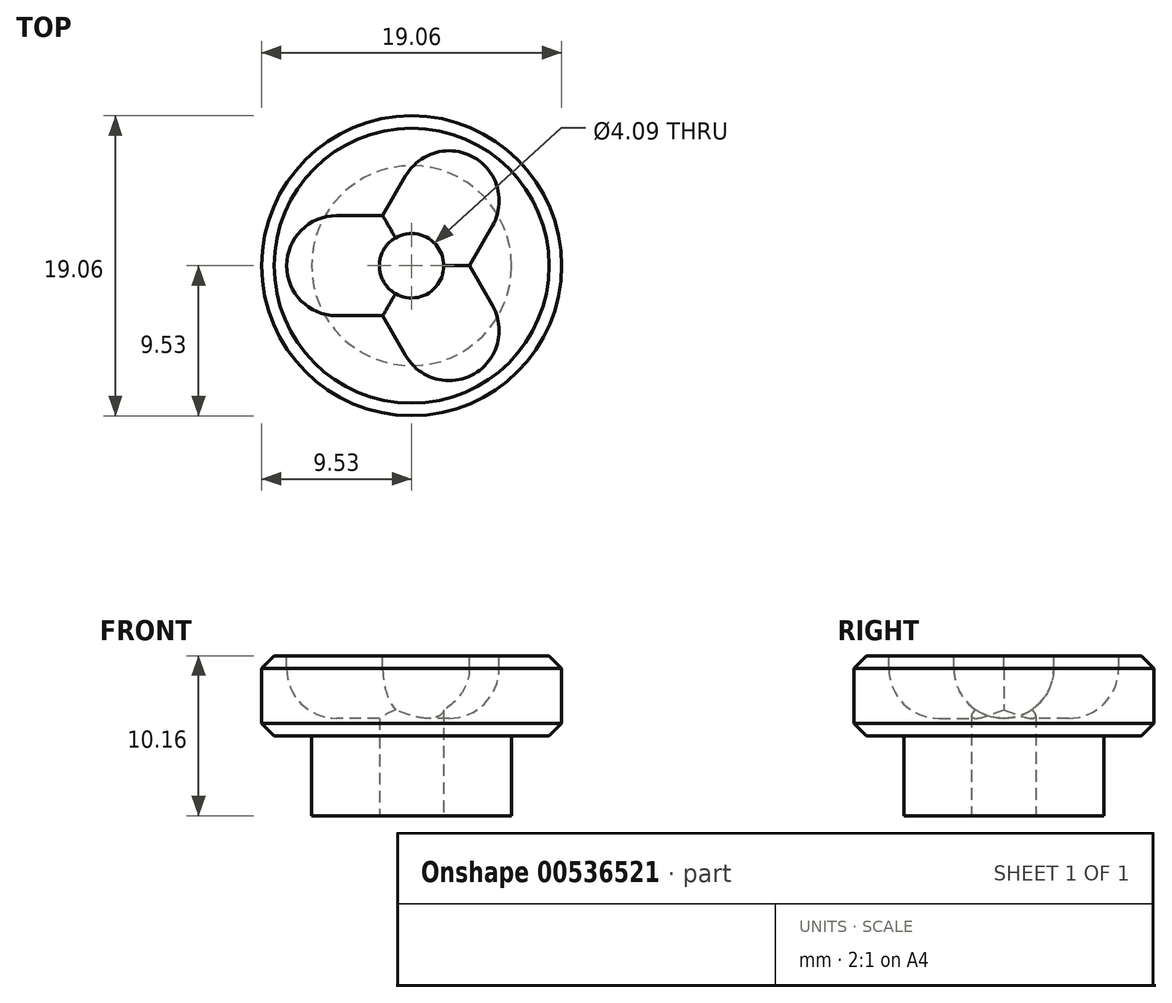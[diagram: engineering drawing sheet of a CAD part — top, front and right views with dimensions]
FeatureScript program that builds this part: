
annotation { "Feature Type Name" : "Feature", "Feature Type Description" : "" }
export const myFeature = defineFeature(function(context is Context, id is Id, definition is map)
    precondition{}
    {
        {
            var Q0;
            Q0=qCreatedBy(makeId("Front.planeOp"),FACE);
            var sketch = newSketch(context, id + "F0", { "sketchPlane" : qUnion([Q0])});
            skLineSegment(sketch, "E0", {"start": v(0, 14.96) * mm, "end": v(0, -17.01) * mm, "construction": true});
            skLineSegment(sketch, "E1", {"start": v(0, -10.16) * mm, "end": v(-6.35, -10.16) * mm});
            skLineSegment(sketch, "E2", {"start": v(-6.35, -10.16) * mm, "end": v(-6.35, -5.08) * mm});
            skLineSegment(sketch, "E3", {"start": v(-6.35, -5.08) * mm, "end": v(-9.52, -5.08) * mm});
            skLineSegment(sketch, "E4", {"start": v(-9.52, -5.08) * mm, "end": v(-9.52, 0) * mm});
            skLineSegment(sketch, "E5", {"start": v(-9.52, 0) * mm, "end": v(0, 0) * mm});
            skLineSegment(sketch, "E6", {"start": v(0, 0) * mm, "end": v(0, -10.16) * mm});
            skCircle(sketch, "E7", {"center": v(0, 4.53) * mm, "radius": 3.97 * mm, "construction": true});
            skCircle(sketch, "E8", {"center": v(-4.76, -0.8) * mm, "radius": 3.18 * mm, "construction": true});
            skLineSegment(sketch, "E9", {"start": v(-7.94, 0) * mm, "end": v(-7.94, -3.97) * mm, "construction": true});
            skLineSegment(sketch, "E10", {"start": v(-7.94, -3.97) * mm, "end": v(0, -3.97) * mm, "construction": true});
            skSolve(sketch);
        }
        {
            var Q0;
            Q0=makeQuery(id+"F0.imprint","IMPRINT",FACE,{"disambiguationData":[TD([[makeQuery(id+"F0.imprint","IMPRINT",EDGE,{"derivedFrom":sQuery(id+"F0.wireOp",EDGE,"E1")}),-1.0]])]});
            var Q1;
            Q1=sQuery(id+"F0.wireOp",EDGE,"E0");
            revolve(context, id + "F1", {"entities" : qUnion([Q0]), "axis" : qUnion([Q1]), "revolveType" : RevolveType.FULL});
        }
        {
            var Q0;
            Q0=makeQuery(id+"F1.opRevolve","SWEPT_EDGE",EDGE,{"disambiguationData":[OSD([sQuery(id+"F0.wireOp",EDGE,"E4"),sQuery(id+"F0.wireOp",EDGE,"E5")])]});
            var Q1;
            Q1=makeQuery(id+"F1.opRevolve","SWEPT_EDGE",EDGE,{"disambiguationData":[OSD([sQuery(id+"F0.wireOp",EDGE,"E3"),sQuery(id+"F0.wireOp",EDGE,"E4")])]});
            chamfer(context, id + "F2", {"entities" : qUnion([Q0, Q1]), "width" : 0.8 * mm, "tangentPropagation" : true});
        }
        {
            var Q0;
            Q0=makeQuery(id+"F1.opRevolve","SWEPT_FACE",FACE,{"disambiguationData":[OSD([sQuery(id+"F0.wireOp",EDGE,"E5")])]});
            var sketch = newSketch(context, id + "F3", { "sketchPlane" : qUnion([Q0])});
            skLineSegment(sketch, "E11", {"start": v(-1.83, -3.18) * mm, "end": v(-4.76, -3.18) * mm});
            skArc(sketch, "E12", {"start": v(-4.76, -3.18) * mm, "mid": v(-7.94, 0) * mm, "end": v(-4.76, 3.17) * mm});
            skLineSegment(sketch, "E13", {"start": v(-4.76, 3.18) * mm, "end": v(-1.83, 3.18) * mm});
            skLineSegment(sketch, "E14", {"start": v(-1.83, 3.18) * mm, "end": v(-0.37, 5.71) * mm});
            skArc(sketch, "E15", {"start": v(-0.37, 5.71) * mm, "mid": v(3.97, 6.87) * mm, "end": v(5.13, 2.54) * mm});
            skLineSegment(sketch, "E16", {"start": v(5.13, 2.54) * mm, "end": v(3.67, 0) * mm});
            skLineSegment(sketch, "E17", {"start": v(3.67, 0) * mm, "end": v(5.13, -2.54) * mm});
            skArc(sketch, "E18", {"start": v(5.13, -2.54) * mm, "mid": v(3.97, -6.87) * mm, "end": v(-0.37, -5.71) * mm});
            skLineSegment(sketch, "E19", {"start": v(-0.37, -5.71) * mm, "end": v(-1.83, -3.18) * mm});
            skLineSegment(sketch, "E20", {"start": v(-4.76, 3.17) * mm, "end": v(-4.76, -3.17) * mm, "construction": true});
            skLineSegment(sketch, "E21", {"start": v(-0.37, -5.71) * mm, "end": v(5.13, -2.54) * mm, "construction": true});
            skLineSegment(sketch, "E22", {"start": v(5.13, 2.54) * mm, "end": v(-0.37, 5.71) * mm, "construction": true});
            skLineSegment(sketch, "E23", {"start": v(-4.76, 0) * mm, "end": v(0, 0) * mm, "construction": true});
            skLineSegment(sketch, "E24", {"start": v(0, 0) * mm, "end": v(2.38, 4.12) * mm, "construction": true});
            skLineSegment(sketch, "E25", {"start": v(0, 0) * mm, "end": v(2.38, -4.12) * mm, "construction": true});
            skSolve(sketch);
        }
        {
            var Q0;
            Q0=makeQuery(id+"F3.imprint","IMPRINT",FACE,{"disambiguationData":[TD([[makeQuery(id+"F3.imprint","IMPRINT",EDGE,{"derivedFrom":sQuery(id+"F3.wireOp",EDGE,"E11")}),-1.0]])]});
            extrude(context, id + "F4", {"entities" : qUnion([Q0]), "operationType" : NewBodyOperationType.REMOVE, "oppositeDirection" : true, "depth" : 3.97 * mm, "offsetDistance" : 25.4 * mm});
        }
        {
            var Q0;
            Q0=makeQuery(id+"F4.boolean.opBoolean","COPY",FACE,{"derivedFrom":makeQuery(id+"F4.opExtrude","CAP_FACE",FACE,{"disambiguationData":[OSD([sQuery(id+"F3.wireOp",EDGE,"E11"),sQuery(id+"F3.wireOp",EDGE,"E12"),sQuery(id+"F3.wireOp",EDGE,"E13"),sQuery(id+"F3.wireOp",EDGE,"E14"),sQuery(id+"F3.wireOp",EDGE,"E15"),sQuery(id+"F3.wireOp",EDGE,"E16"),sQuery(id+"F3.wireOp",EDGE,"E17"),sQuery(id+"F3.wireOp",EDGE,"E18"),sQuery(id+"F3.wireOp",EDGE,"E19")])],"isStart":false})});
            fillet(context, id + "F5", {"entities" : qUnion([Q0]), "radius" : 3.17 * mm, "tangentPropagation" : true, "allowEdgeOverflow" : false});
        }
        {
            var Q0;
            Q0=makeQuery(id+"F1.opRevolve","SWEPT_FACE",FACE,{"disambiguationData":[OSD([sQuery(id+"F0.wireOp",EDGE,"E1")])]});
            var sketch = newSketch(context, id + "F6", { "sketchPlane" : qUnion([Q0])});
            skPoint(sketch, "E26", {"position": v(0, 0) * mm});
            skSolve(sketch);
        }
        {
            var Q0;
            Q0=sQuery(id+"F6.wireOp",VERTEX,"E26");
            var Q1;
            Q1=makeQuery(id+"F1.opRevolve","SWEPT_BODY",BODY,{"disambiguationData":[OSD([sQuery(id+"F0.wireOp",EDGE,"E1"),sQuery(id+"F0.wireOp",EDGE,"E2"),sQuery(id+"F0.wireOp",EDGE,"E3"),sQuery(id+"F0.wireOp",EDGE,"E4"),sQuery(id+"F0.wireOp",EDGE,"E5"),sQuery(id+"F0.wireOp",EDGE,"E6")])]});
            hole(context, id + "F7", {"style" : HoleStyle.SIMPLE, "endStyle" : HoleEndStyle.THROUGH, "standardTappedOrClearance" : lookupTablePath({ "standard" : "ANSI", "size" : "#20 (0.16)", "type" : "Drilled" }), "standardBlindInLast" : lookupTablePath({ "standard" : "ANSI", "size" : "#20", "type" : "Drilled" }), "holeDiameter" : 4.1 * mm, "majorDiameter" : 6.35 * mm, "isTappedThrough" : true, "tappedDepth" : 15.88 * mm, "tapClearance" : 3, "startFromSketch" : true, "locations" : qUnion([Q0]), "scope" : qUnion([Q1])});
        }
    });
